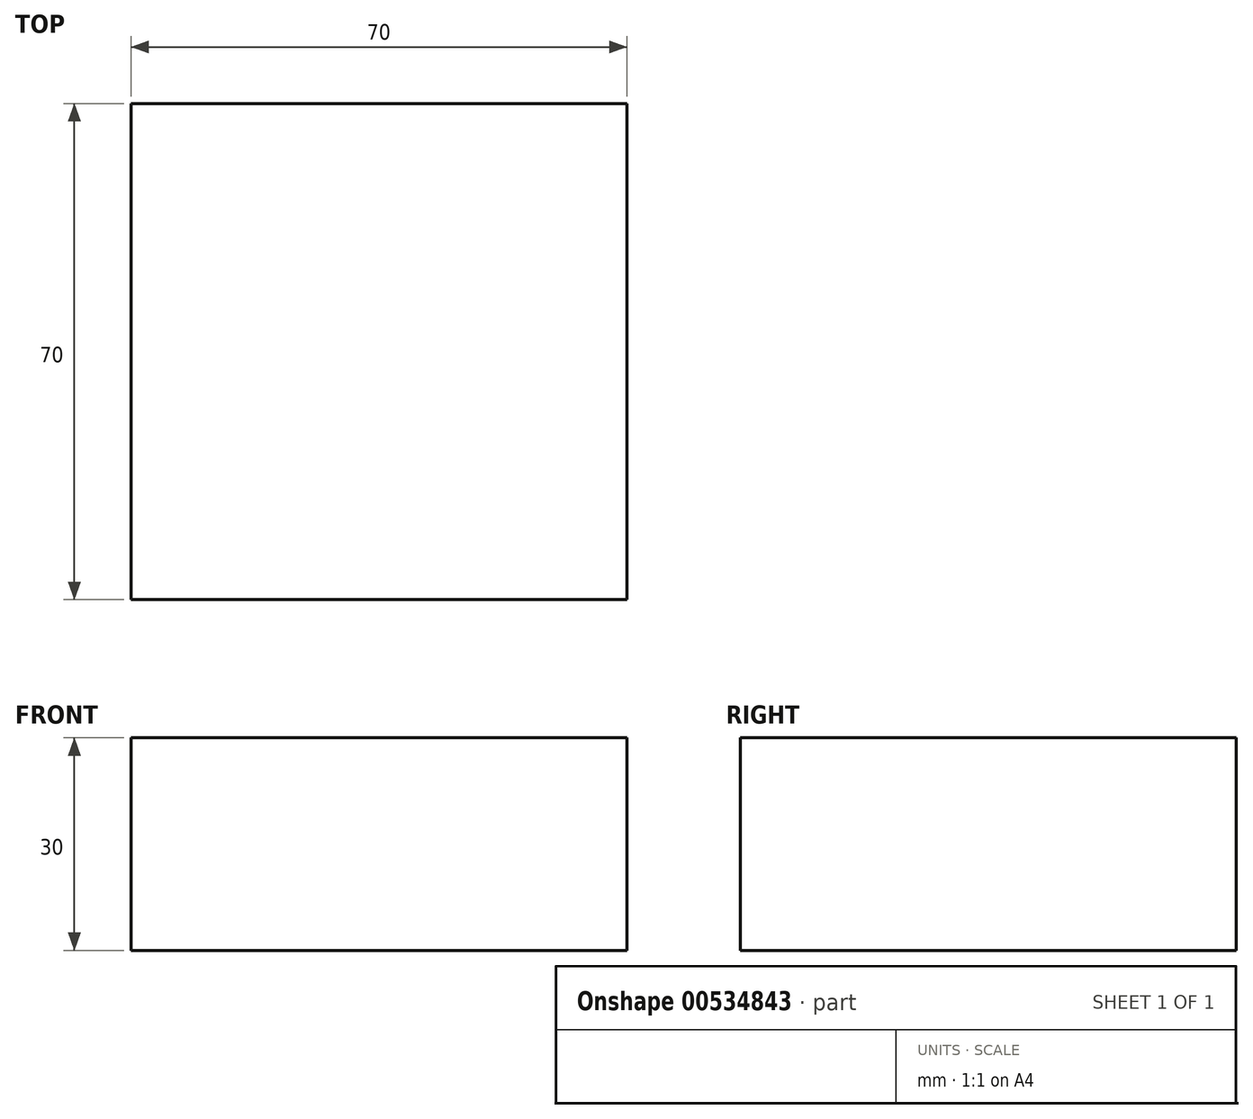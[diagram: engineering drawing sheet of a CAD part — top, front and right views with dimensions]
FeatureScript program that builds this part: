
annotation { "Feature Type Name" : "Feature", "Feature Type Description" : "" }
export const myFeature = defineFeature(function(context is Context, id is Id, definition is map)
    precondition{}
    {
        {
            var Q0;
            Q0=qCreatedBy(makeId("Top.planeOp"),FACE);
            var sketch = newSketch(context, id + "F0", { "sketchPlane" : qUnion([Q0])});
            skLineSegment(sketch, "E0.bottom", {"start": v(35, -35) * mm, "end": v(-35, -35) * mm});
            skLineSegment(sketch, "E0.top", {"start": v(35, 35) * mm, "end": v(-35, 35) * mm});
            skLineSegment(sketch, "E0.left", {"start": v(35, -35) * mm, "end": v(35, 35) * mm});
            skLineSegment(sketch, "E0.right", {"start": v(-35, -35) * mm, "end": v(-35, 35) * mm});
            skPoint(sketch, "E0.middle", {"position": v(0, 0) * mm});
            skSolve(sketch);
        }
        {
            var Q0;
            Q0=makeQuery(id+"F0.imprint","IMPRINT",FACE,{"disambiguationData":[TD([[makeQuery(id+"F0.imprint","IMPRINT",EDGE,{"derivedFrom":sQuery(id+"F0.wireOp",EDGE,"E0.bottom")}),-1.0]])]});
            extrude(context, id + "F1", {"entities" : qUnion([Q0]), "depth" : 30 * mm, "offsetDistance" : 25 * mm});
        }
    });
